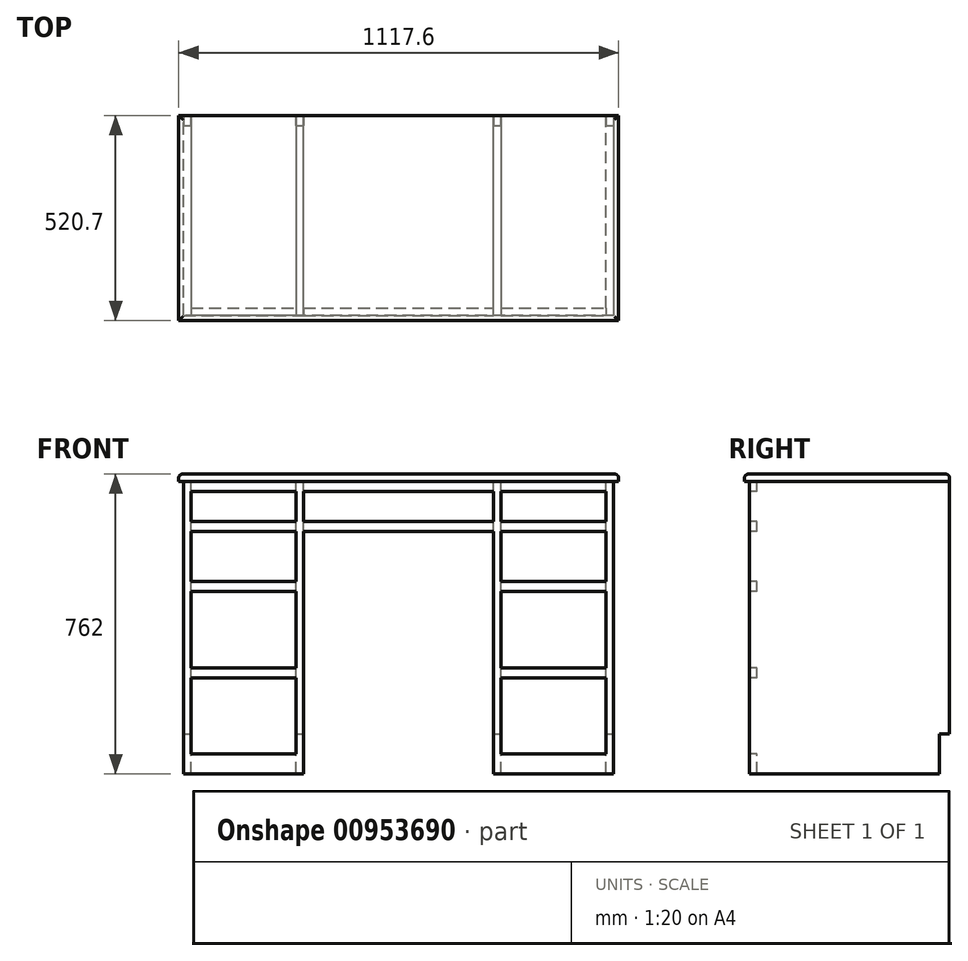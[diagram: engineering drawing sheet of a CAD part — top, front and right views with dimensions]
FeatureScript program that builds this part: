
annotation { "Feature Type Name" : "Feature", "Feature Type Description" : "" }
export const myFeature = defineFeature(function(context is Context, id is Id, definition is map)
    precondition{}
    {
        {
            var Q0;
            Q0=qCreatedBy(makeId("Top.planeOp"),FACE);
            var sketch = newSketch(context, id + "F0", { "sketchPlane" : qUnion([Q0])});
            skLineSegment(sketch, "E0.bottom", {"start": v(-553.55, -267.41) * mm, "end": v(564.05, -267.41) * mm});
            skLineSegment(sketch, "E0.top", {"start": v(-553.55, 253.29) * mm, "end": v(564.05, 253.29) * mm});
            skLineSegment(sketch, "E0.left", {"start": v(-553.55, -267.41) * mm, "end": v(-553.55, 253.29) * mm});
            skLineSegment(sketch, "E0.right", {"start": v(564.05, -267.41) * mm, "end": v(564.05, 253.29) * mm});
            skLineSegment(sketch, "E1", {"start": v(-553.55, 253.29) * mm, "end": v(-521.8, 253.29) * mm});
            skLineSegment(sketch, "E2", {"start": v(-521.8, 253.29) * mm, "end": v(-521.8, -254.71) * mm});
            skLineSegment(sketch, "E3", {"start": v(-521.8, -254.71) * mm, "end": v(-540.85, -254.71) * mm});
            skLineSegment(sketch, "E4", {"start": v(-540.85, -254.71) * mm, "end": v(-540.85, 253.29) * mm});
            skLineSegment(sketch, "E5", {"start": v(-255.1, 253.29) * mm, "end": v(-255.1, -254.71) * mm});
            skLineSegment(sketch, "E6", {"start": v(-255.1, -254.71) * mm, "end": v(-236.05, -254.71) * mm});
            skLineSegment(sketch, "E7", {"start": v(-236.05, -254.71) * mm, "end": v(-236.05, 253.29) * mm});
            skLineSegment(sketch, "E8", {"start": v(551.35, 253.29) * mm, "end": v(551.35, -254.71) * mm});
            skLineSegment(sketch, "E9", {"start": v(551.35, -254.71) * mm, "end": v(532.3, -254.71) * mm});
            skLineSegment(sketch, "E10", {"start": v(532.3, -254.71) * mm, "end": v(532.3, 253.29) * mm});
            skLineSegment(sketch, "E11", {"start": v(265.6, 253.29) * mm, "end": v(265.6, -254.71) * mm});
            skLineSegment(sketch, "E12", {"start": v(265.6, -254.71) * mm, "end": v(246.55, -254.71) * mm});
            skLineSegment(sketch, "E13", {"start": v(246.55, -254.71) * mm, "end": v(246.55, 253.29) * mm});
            skLineSegment(sketch, "E14", {"start": v(-236.05, -254.71) * mm, "end": v(246.55, -254.71) * mm});
            skLineSegment(sketch, "E15", {"start": v(-236.05, -235.66) * mm, "end": v(246.55, -235.66) * mm});
            skLineSegment(sketch, "E16", {"start": v(265.6, -235.66) * mm, "end": v(532.3, -235.66) * mm});
            skLineSegment(sketch, "E17", {"start": v(532.3, -254.71) * mm, "end": v(265.6, -254.71) * mm});
            skLineSegment(sketch, "E18", {"start": v(-255.1, -254.71) * mm, "end": v(-521.8, -254.71) * mm});
            skLineSegment(sketch, "E19", {"start": v(-255.1, -235.66) * mm, "end": v(-521.8, -235.66) * mm});
            skSolve(sketch);
        }
        {
            var Q0;
            {var subQ5=sQuery(id+"F0.wireOp",EDGE,"E19");var subQ10=sQuery(id+"F0.wireOp",EDGE,"E6");var subQ11=makeQuery(id+"F0.imprint","IMPRINT",EDGE,{"derivedFrom":subQ10});var subQ15=sQuery(id+"F0.wireOp",EDGE,"E15");var subQ23=sQuery(id+"F0.wireOp",EDGE,"E16");var subQ28=sQuery(id+"F0.wireOp",EDGE,"E3");var subQ29=makeQuery(id+"F0.imprint","IMPRINT",EDGE,{"derivedFrom":subQ28});var subQ40=sQuery(id+"F0.wireOp",EDGE,"E8");var subQ41=makeQuery(id+"F0.imprint","IMPRINT",EDGE,{"derivedFrom":subQ40});var subQ45=sQuery(id+"F0.wireOp",EDGE,"E12");var subQ46=makeQuery(id+"F0.imprint","IMPRINT",EDGE,{"derivedFrom":subQ45});Q0=qUnion([makeQuery(id+"F0.imprint","IMPRINT",FACE,{"disambiguationData":[TD([[subQ46,-1.0]])]}),makeQuery(id+"F0.imprint","IMPRINT",FACE,{"disambiguationData":[TD([[subQ41,-1.0]])]}),makeQuery(id+"F0.imprint","IMPRINT",FACE,{"disambiguationData":[TD([[makeQuery(id+"F0.imprint","IMPRINT",EDGE,{"derivedFrom":sQuery(id+"F0.wireOp",EDGE,"E0.bottom")}),1.0]])]}),makeQuery(id+"F0.imprint","IMPRINT",FACE,{"disambiguationData":[TD([[makeQuery(id+"F0.imprint","IMPRINT",EDGE,{"derivedFrom":subQ15}),1.0]])]}),makeQuery(id+"F0.imprint","IMPRINT",FACE,{"disambiguationData":[TD([[subQ29,-1.0]])]}),makeQuery(id+"F0.imprint","IMPRINT",FACE,{"disambiguationData":[TD([[makeQuery(id+"F0.imprint","IMPRINT",EDGE,{"derivedFrom":subQ23}),1.0]])]}),makeQuery(id+"F0.imprint","IMPRINT",FACE,{"disambiguationData":[TD([[subQ11,1.0]])]}),makeQuery(id+"F0.imprint","IMPRINT",FACE,{"disambiguationData":[TD([[makeQuery(id+"F0.imprint","IMPRINT",EDGE,{"derivedFrom":subQ5}),-1.0]])]})]);}
            var Q1;
            {var subQ0=sQuery(id+"F0.wireOp",EDGE,"E18");Q1=makeQuery(id+"F0.imprint","IMPRINT",FACE,{"disambiguationData":[TD([[makeQuery(id+"F0.imprint","IMPRINT",EDGE,{"derivedFrom":subQ0}),-1.0]])]});}
            var Q2;
            {var subQ0=sQuery(id+"F0.wireOp",EDGE,"E14");Q2=makeQuery(id+"F0.imprint","IMPRINT",FACE,{"disambiguationData":[TD([[makeQuery(id+"F0.imprint","IMPRINT",EDGE,{"derivedFrom":subQ0}),1.0]])]});}
            var Q3;
            {var subQ2=sQuery(id+"F0.wireOp",EDGE,"E16");Q3=makeQuery(id+"F0.imprint","IMPRINT",FACE,{"disambiguationData":[TD([[makeQuery(id+"F0.imprint","IMPRINT",EDGE,{"derivedFrom":subQ2}),-1.0]])]});}
            extrude(context, id + "F1", {"entities" : qUnion([Q0, Q1, Q2, Q3]), "depth" : 19.05 * mm, "offsetDistance" : 25.4 * mm});
        }
        {
            var Q0;
            {var subQ0=sQuery(id+"F0.wireOp",EDGE,"E3");Q0=makeQuery(id+"F0.imprint","IMPRINT",FACE,{"disambiguationData":[TD([[makeQuery(id+"F0.imprint","IMPRINT",EDGE,{"derivedFrom":subQ0}),-1.0]])]});}
            var Q1;
            {var subQ0=sQuery(id+"F0.wireOp",EDGE,"E6");Q1=makeQuery(id+"F0.imprint","IMPRINT",FACE,{"disambiguationData":[TD([[makeQuery(id+"F0.imprint","IMPRINT",EDGE,{"derivedFrom":subQ0}),1.0]])]});}
            var Q2;
            {var subQ0=sQuery(id+"F0.wireOp",EDGE,"E12");Q2=makeQuery(id+"F0.imprint","IMPRINT",FACE,{"disambiguationData":[TD([[makeQuery(id+"F0.imprint","IMPRINT",EDGE,{"derivedFrom":subQ0}),-1.0]])]});}
            var Q3;
            {var subQ5=sQuery(id+"F0.wireOp",EDGE,"E8");Q3=makeQuery(id+"F0.imprint","IMPRINT",FACE,{"disambiguationData":[TD([[makeQuery(id+"F0.imprint","IMPRINT",EDGE,{"derivedFrom":subQ5}),-1.0]])]});}
            extrude(context, id + "F2", {"entities" : qUnion([Q0, Q1, Q2, Q3]), "operationType" : NewBodyOperationType.ADD, "oppositeDirection" : true, "depth" : 742.95 * mm, "offsetDistance" : 25.4 * mm});
        }
        {
            var Q0;
            {var subQ0=sQuery(id+"F0.wireOp",EDGE,"E18");Q0=makeQuery(id+"F0.imprint","IMPRINT",FACE,{"disambiguationData":[TD([[makeQuery(id+"F0.imprint","IMPRINT",EDGE,{"derivedFrom":subQ0}),-1.0]])]});}
            var Q1;
            {var subQ2=sQuery(id+"F0.wireOp",EDGE,"E16");Q1=makeQuery(id+"F0.imprint","IMPRINT",FACE,{"disambiguationData":[TD([[makeQuery(id+"F0.imprint","IMPRINT",EDGE,{"derivedFrom":subQ2}),-1.0]])]});}
            extrude(context, id + "F3", {"entities" : qUnion([Q0, Q1]), "operationType" : NewBodyOperationType.ADD, "oppositeDirection" : true, "depth" : 742.95 * mm, "offsetDistance" : 25.4 * mm});
        }
        {
            var Q0;
            Q0=makeQuery(id+"F1.opExtrude","CAP_FACE",FACE,{"disambiguationData":[OSD([sQuery(id+"F0.wireOp",EDGE,"E0.bottom"),sQuery(id+"F0.wireOp",EDGE,"E0.top"),sQuery(id+"F0.wireOp",EDGE,"E0.left"),sQuery(id+"F0.wireOp",EDGE,"E0.right")])],"isStart":false});
            fillet(context, id + "F4", {"entities" : qUnion([Q0]), "radius" : 10.16 * mm, "tangentPropagation" : true, "allowEdgeOverflow" : false});
        }
        {
            var Q0;
            {var subQ0=sQuery(id+"F0.wireOp",EDGE,"E14");Q0=makeQuery(id+"F0.imprint","IMPRINT",FACE,{"disambiguationData":[TD([[makeQuery(id+"F0.imprint","IMPRINT",EDGE,{"derivedFrom":subQ0}),1.0]])]});}
            extrude(context, id + "F5", {"entities" : qUnion([Q0]), "operationType" : NewBodyOperationType.ADD, "oppositeDirection" : true, "depth" : 127 * mm, "offsetDistance" : 25.4 * mm});
        }
        {
            var Q0;
            Q0=makeQuery(id+"F5.boolean.opBoolean","MERGE",FACE,{"derivedFrom":[makeQuery(id+"F3.boolean.opBoolean","MERGE",FACE,{"derivedFrom":[makeQuery(id+"F2.opExtrude","SWEPT_FACE",FACE,{"disambiguationData":[OSD([sQuery(id+"F0.wireOp",EDGE,"E3")])]}),makeQuery(id+"F2.opExtrude","SWEPT_FACE",FACE,{"disambiguationData":[OSD([sQuery(id+"F0.wireOp",EDGE,"E6")])]}),makeQuery(id+"F3.opExtrude","SWEPT_FACE",FACE,{"disambiguationData":[OSD([sQuery(id+"F0.wireOp",EDGE,"E18")])]})]}),makeQuery(id+"F3.boolean.opBoolean","MERGE",FACE,{"derivedFrom":[makeQuery(id+"F2.opExtrude","SWEPT_FACE",FACE,{"disambiguationData":[OSD([sQuery(id+"F0.wireOp",EDGE,"E9")])]}),makeQuery(id+"F2.opExtrude","SWEPT_FACE",FACE,{"disambiguationData":[OSD([sQuery(id+"F0.wireOp",EDGE,"E12")])]}),makeQuery(id+"F3.opExtrude","SWEPT_FACE",FACE,{"disambiguationData":[OSD([sQuery(id+"F0.wireOp",EDGE,"E17")])]})]}),makeQuery(id+"F5.opExtrude","SWEPT_FACE",FACE,{"disambiguationData":[OSD([sQuery(id+"F0.wireOp",EDGE,"E14")])]})]});
            var sketch = newSketch(context, id + "F6", { "sketchPlane" : qUnion([Q0])});
            skLineSegment(sketch, "E20", {"start": v(-236.05, -127) * mm, "end": v(-236.05, -101.6) * mm});
            skLineSegment(sketch, "E21", {"start": v(-236.05, -101.6) * mm, "end": v(246.55, -101.6) * mm});
            skLineSegment(sketch, "E22", {"start": v(246.55, -101.6) * mm, "end": v(246.55, -127) * mm});
            skLineSegment(sketch, "E23", {"start": v(-236.05, 0) * mm, "end": v(-236.05, -25.4) * mm});
            skLineSegment(sketch, "E24", {"start": v(-236.05, -25.4) * mm, "end": v(246.55, -25.4) * mm});
            skLineSegment(sketch, "E25", {"start": v(246.55, -25.4) * mm, "end": v(246.55, 0) * mm});
            skLineSegment(sketch, "E26", {"start": v(-236.05, -101.6) * mm, "end": v(-236.05, -25.4) * mm});
            skLineSegment(sketch, "E27", {"start": v(246.55, -101.6) * mm, "end": v(246.55, -25.4) * mm});
            skLineSegment(sketch, "E28", {"start": v(-521.8, -742.95) * mm, "end": v(-521.8, -692.15) * mm});
            skLineSegment(sketch, "E29", {"start": v(-521.8, -692.15) * mm, "end": v(-255.1, -692.15) * mm});
            skLineSegment(sketch, "E30", {"start": v(-255.1, -692.15) * mm, "end": v(-255.1, -742.95) * mm});
            skLineSegment(sketch, "E31", {"start": v(-521.8, 0) * mm, "end": v(-521.8, -25.4) * mm});
            skLineSegment(sketch, "E32", {"start": v(-521.8, -25.4) * mm, "end": v(-255.1, -25.4) * mm});
            skLineSegment(sketch, "E33", {"start": v(-255.1, -25.4) * mm, "end": v(-255.1, 0) * mm});
            skLineSegment(sketch, "E34", {"start": v(-521.8, -25.4) * mm, "end": v(-521.8, -692.15) * mm});
            skLineSegment(sketch, "E35", {"start": v(-255.1, -692.15) * mm, "end": v(-255.1, -25.4) * mm});
            skLineSegment(sketch, "E36", {"start": v(-255.1, -101.6) * mm, "end": v(-521.8, -101.6) * mm});
            skLineSegment(sketch, "E37", {"start": v(-255.1, -127) * mm, "end": v(-521.8, -127) * mm});
            skLineSegment(sketch, "E38", {"start": v(265.6, 0) * mm, "end": v(265.6, -742.95) * mm});
            skLineSegment(sketch, "E39", {"start": v(532.3, -742.95) * mm, "end": v(532.3, 0) * mm});
            skLineSegment(sketch, "E40", {"start": v(265.6, -25.4) * mm, "end": v(532.3, -25.4) * mm});
            skLineSegment(sketch, "E41", {"start": v(265.6, -692.15) * mm, "end": v(532.3, -692.15) * mm});
            skLineSegment(sketch, "E42", {"start": v(-521.8, -498.48) * mm, "end": v(-255.1, -498.48) * mm});
            skLineSegment(sketch, "E43", {"start": v(-255.1, -473.08) * mm, "end": v(-521.8, -473.08) * mm});
            skLineSegment(sketch, "E44", {"start": v(-255.1, -279.4) * mm, "end": v(-521.8, -279.4) * mm});
            skLineSegment(sketch, "E45", {"start": v(-255.1, -254) * mm, "end": v(-521.8, -254) * mm});
            skLineSegment(sketch, "E46", {"start": v(265.6, -254) * mm, "end": v(532.3, -254) * mm});
            skLineSegment(sketch, "E47", {"start": v(265.6, -279.4) * mm, "end": v(532.3, -279.4) * mm});
            skLineSegment(sketch, "E48", {"start": v(265.6, -101.6) * mm, "end": v(532.3, -101.6) * mm});
            skLineSegment(sketch, "E49", {"start": v(265.6, -127) * mm, "end": v(532.3, -127) * mm});
            skLineSegment(sketch, "E50", {"start": v(265.6, -473.08) * mm, "end": v(532.3, -473.08) * mm});
            skLineSegment(sketch, "E51", {"start": v(265.6, -498.48) * mm, "end": v(532.3, -498.48) * mm});
            skSolve(sketch);
        }
        {
            var Q0;
            {var subQ0=sQuery(id+"F6.wireOp",EDGE,"E29");Q0=makeQuery(id+"F6.imprint","IMPRINT",FACE,{"disambiguationData":[TD([[makeQuery(id+"F6.imprint","IMPRINT",EDGE,{"derivedFrom":subQ0}),1.0]])]});}
            var Q1;
            {var subQ0=sQuery(id+"F6.wireOp",EDGE,"E43");Q1=makeQuery(id+"F6.imprint","IMPRINT",FACE,{"disambiguationData":[TD([[makeQuery(id+"F6.imprint","IMPRINT",EDGE,{"derivedFrom":subQ0}),-1.0]])]});}
            var Q2;
            {var subQ0=sQuery(id+"F6.wireOp",EDGE,"E37");Q2=makeQuery(id+"F6.imprint","IMPRINT",FACE,{"disambiguationData":[TD([[makeQuery(id+"F6.imprint","IMPRINT",EDGE,{"derivedFrom":subQ0}),1.0]])]});}
            var Q3;
            {var subQ0=sQuery(id+"F6.wireOp",EDGE,"E32");Q3=makeQuery(id+"F6.imprint","IMPRINT",FACE,{"disambiguationData":[TD([[makeQuery(id+"F6.imprint","IMPRINT",EDGE,{"derivedFrom":subQ0}),-1.0]])]});}
            var Q4;
            Q4=makeQuery(id+"F6.imprint","IMPRINT",FACE,{"disambiguationData":[TD([[makeQuery(id+"F6.imprint","IMPRINT",EDGE,{"derivedFrom":sQuery(id+"F6.wireOp",EDGE,"E21")}),1.0]])]});
            var Q5;
            {var subQ0=sQuery(id+"F6.wireOp",EDGE,"E40");Q5=makeQuery(id+"F6.imprint","IMPRINT",FACE,{"disambiguationData":[TD([[makeQuery(id+"F6.imprint","IMPRINT",EDGE,{"derivedFrom":subQ0}),-1.0]])]});}
            var Q6;
            {var subQ0=sQuery(id+"F6.wireOp",EDGE,"E46");Q6=makeQuery(id+"F6.imprint","IMPRINT",FACE,{"disambiguationData":[TD([[makeQuery(id+"F6.imprint","IMPRINT",EDGE,{"derivedFrom":subQ0}),1.0]])]});}
            var Q7;
            {var subQ0=sQuery(id+"F6.wireOp",EDGE,"E47");Q7=makeQuery(id+"F6.imprint","IMPRINT",FACE,{"disambiguationData":[TD([[makeQuery(id+"F6.imprint","IMPRINT",EDGE,{"derivedFrom":subQ0}),-1.0]])]});}
            var Q8;
            {var subQ0=sQuery(id+"F6.wireOp",EDGE,"E41");Q8=makeQuery(id+"F6.imprint","IMPRINT",FACE,{"disambiguationData":[TD([[makeQuery(id+"F6.imprint","IMPRINT",EDGE,{"derivedFrom":subQ0}),1.0]])]});}
            extrude(context, id + "F7", {"entities" : qUnion([Q0, Q1, Q2, Q3, Q4, Q5, Q6, Q7, Q8]), "operationType" : NewBodyOperationType.REMOVE, "oppositeDirection" : true, "depth" : 25.4 * mm, "offsetDistance" : 25.4 * mm});
        }
        {
            var Q0;
            Q0=makeQuery(id+"F2.opExtrude","SWEPT_FACE",FACE,{"disambiguationData":[OSD([sQuery(id+"F0.wireOp",EDGE,"E8")])]});
            var sketch = newSketch(context, id + "F8", { "sketchPlane" : qUnion([Q0])});
            skLineSegment(sketch, "E52.bottom", {"start": v(253.29, -742.95) * mm, "end": v(227.89, -742.95) * mm});
            skLineSegment(sketch, "E52.top", {"start": v(253.29, -641.35) * mm, "end": v(227.89, -641.35) * mm});
            skLineSegment(sketch, "E52.left", {"start": v(253.29, -742.95) * mm, "end": v(253.29, -641.35) * mm});
            skLineSegment(sketch, "E52.right", {"start": v(227.89, -742.95) * mm, "end": v(227.89, -641.35) * mm});
            skSolve(sketch);
        }
        {
            var Q0;
            Q0 = qSketchRegion(id + "F8", true);
            extrude(context, id + "F9", {"entities" : qUnion([Q0]), "operationType" : NewBodyOperationType.REMOVE, "endBound" : BoundingType.THROUGH_ALL, "oppositeDirection" : true, "depth" : 25.4 * mm, "offsetDistance" : 25.4 * mm});
        }
    });
